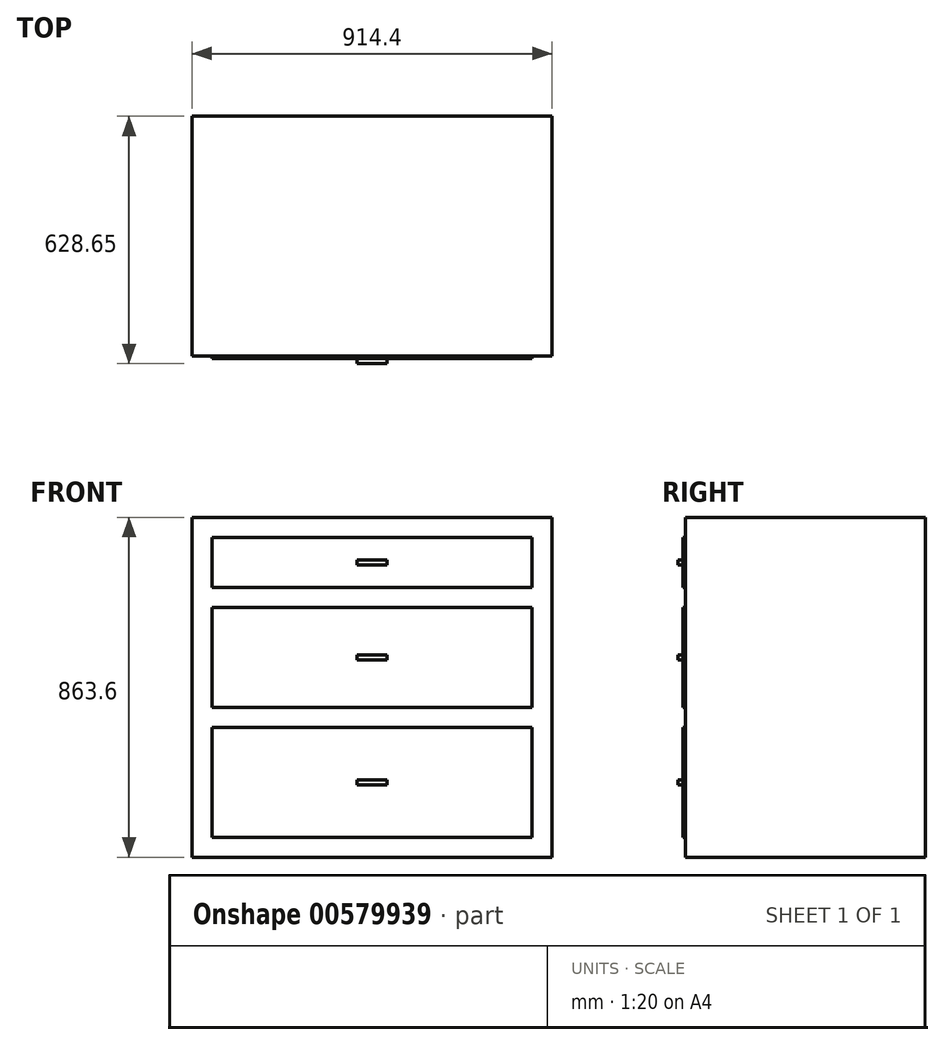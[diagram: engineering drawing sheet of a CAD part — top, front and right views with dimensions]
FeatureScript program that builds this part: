
annotation { "Feature Type Name" : "Feature", "Feature Type Description" : "" }
export const myFeature = defineFeature(function(context is Context, id is Id, definition is map)
    precondition{}
    {
        {
            var Q0;
            Q0=qCreatedBy(makeId("Front.planeOp"),FACE);
            var sketch = newSketch(context, id + "F0", { "sketchPlane" : qUnion([Q0])});
            skLineSegment(sketch, "E0.bottom", {"start": v(-473.14, 610.22) * mm, "end": v(441.26, 610.22) * mm});
            skLineSegment(sketch, "E0.top", {"start": v(-473.14, -253.38) * mm, "end": v(441.26, -253.38) * mm});
            skLineSegment(sketch, "E0.left", {"start": v(-473.14, 610.22) * mm, "end": v(-473.14, -253.38) * mm});
            skLineSegment(sketch, "E0.right", {"start": v(441.26, 610.22) * mm, "end": v(441.26, -253.38) * mm});
            skSolve(sketch);
        }
        {
            var Q0;
            Q0 = qSketchRegion(id + "F0", true);
            extrude(context, id + "F1", {"entities" : qUnion([Q0]), "depth" : 609.6 * mm, "offsetDistance" : 25.4 * mm});
        }
        {
            var Q0;
            Q0=makeQuery(id+"F1.opExtrude","CAP_FACE",FACE,{"disambiguationData":[OSD([sQuery(id+"F0.wireOp",EDGE,"E0.bottom"),sQuery(id+"F0.wireOp",EDGE,"E0.top"),sQuery(id+"F0.wireOp",EDGE,"E0.left"),sQuery(id+"F0.wireOp",EDGE,"E0.right")])],"isStart":false});
            var sketch = newSketch(context, id + "F2", { "sketchPlane" : qUnion([Q0])});
            skLineSegment(sketch, "E1.bottom", {"start": v(-422.34, 559.42) * mm, "end": v(390.46, 559.42) * mm});
            skLineSegment(sketch, "E1.top", {"start": v(-422.34, 432.42) * mm, "end": v(390.46, 432.42) * mm});
            skLineSegment(sketch, "E1.left", {"start": v(-422.34, 559.42) * mm, "end": v(-422.34, 432.42) * mm});
            skLineSegment(sketch, "E1.right", {"start": v(390.46, 559.42) * mm, "end": v(390.46, 432.42) * mm});
            skLineSegment(sketch, "E2.bottom", {"start": v(-422.34, 381.62) * mm, "end": v(390.46, 381.62) * mm});
            skLineSegment(sketch, "E2.top", {"start": v(-422.34, 127.62) * mm, "end": v(390.46, 127.62) * mm});
            skLineSegment(sketch, "E2.left", {"start": v(-422.34, 381.62) * mm, "end": v(-422.34, 127.62) * mm});
            skLineSegment(sketch, "E2.right", {"start": v(390.46, 381.62) * mm, "end": v(390.46, 127.62) * mm});
            skLineSegment(sketch, "E3.bottom", {"start": v(-422.34, 76.82) * mm, "end": v(390.46, 76.82) * mm});
            skLineSegment(sketch, "E3.top", {"start": v(-422.34, -202.58) * mm, "end": v(390.46, -202.58) * mm});
            skLineSegment(sketch, "E3.left", {"start": v(-422.34, 76.82) * mm, "end": v(-422.34, -202.58) * mm});
            skLineSegment(sketch, "E3.right", {"start": v(390.46, 76.82) * mm, "end": v(390.46, -202.58) * mm});
            skSolve(sketch);
        }
        {
            var Q0;
            Q0 = qSketchRegion(id + "F2", true);
            extrude(context, id + "F3", {"entities" : qUnion([Q0]), "operationType" : NewBodyOperationType.ADD, "depth" : 6.35 * mm, "offsetDistance" : 25.4 * mm});
        }
        {
            var Q0;
            Q0=makeQuery(id+"F3.opExtrude","CAP_FACE",FACE,{"disambiguationData":[OSD([sQuery(id+"F2.wireOp",EDGE,"E1.bottom"),sQuery(id+"F2.wireOp",EDGE,"E1.top"),sQuery(id+"F2.wireOp",EDGE,"E1.left"),sQuery(id+"F2.wireOp",EDGE,"E1.right")])],"isStart":false});
            var sketch = newSketch(context, id + "F4", { "sketchPlane" : qUnion([Q0])});
            skLineSegment(sketch, "E4.bottom", {"start": v(-54.04, 502.27) * mm, "end": v(22.16, 502.27) * mm});
            skLineSegment(sketch, "E4.top", {"start": v(-54.04, 489.57) * mm, "end": v(22.16, 489.57) * mm});
            skLineSegment(sketch, "E4.left", {"start": v(-54.04, 502.27) * mm, "end": v(-54.04, 489.57) * mm});
            skLineSegment(sketch, "E4.right", {"start": v(22.16, 502.27) * mm, "end": v(22.16, 489.57) * mm});
            skLineSegment(sketch, "E5.bottom", {"start": v(-54.04, 260.97) * mm, "end": v(22.16, 260.97) * mm});
            skLineSegment(sketch, "E5.top", {"start": v(-54.04, 248.27) * mm, "end": v(22.16, 248.27) * mm});
            skLineSegment(sketch, "E5.left", {"start": v(-54.04, 260.97) * mm, "end": v(-54.04, 248.27) * mm});
            skLineSegment(sketch, "E5.right", {"start": v(22.16, 260.97) * mm, "end": v(22.16, 248.27) * mm});
            skLineSegment(sketch, "E6.bottom", {"start": v(-54.04, -56.53) * mm, "end": v(22.16, -56.53) * mm});
            skLineSegment(sketch, "E6.top", {"start": v(-54.04, -69.23) * mm, "end": v(22.16, -69.23) * mm});
            skLineSegment(sketch, "E6.left", {"start": v(-54.04, -56.53) * mm, "end": v(-54.04, -69.23) * mm});
            skLineSegment(sketch, "E6.right", {"start": v(22.16, -56.53) * mm, "end": v(22.16, -69.23) * mm});
            skSolve(sketch);
        }
        {
            var Q0;
            Q0 = qSketchRegion(id + "F4", true);
            extrude(context, id + "F5", {"entities" : qUnion([Q0]), "operationType" : NewBodyOperationType.ADD, "depth" : 12.7 * mm, "offsetDistance" : 25.4 * mm});
        }
    });
